# Revit family: SLIM INGROUND 6W SIMETRICO_LKB0326WW.15
name_source: partatom
category: Luminarias
units: mm (PartAtom-declared; Revit-internal decimal feet)

## family parameters
Compartido = No
Corte con vacíos al cargar = No
Cota de conector redondo = Diámetro de uso
Origen de luz = Sí
Punto de cálculo de habitación = No
Se basa en plano de trabajo = Sí
Siempre vertical = No
Tipo de pieza = Normal

## types (1)
- EMP_LKB0326WW.15
    Cambio de temperatura de color de luz atenuada = <Ninguno>
    Comentarios de vataje = 100-240V
    Descripción = LUMINARIA TIPO CIRCULAR PARA EMPOTRAR EN PISO CON CUERPO DE ALUMINIO FUNDIDO A PRESION CUBIERTO CON POLVO GRIS OSCURO, CON CUBIERTA DE ACERO INOXIDABLE Y VIDRIO TEMPLADO DE 8MM, CON 116MM DE DIAMETRO Y 38MM DE PROFUNDIDAD, INSTALACION EMPOTRABLE EN PISO CON POCO ESPACIO, USO PARA INTERIORES COMO EXTERIORES CON IP 67, CUENTA CON 3 LED TIPO OSRAM CON UNA POTENCIA TOTAL DE 6.2W, A UNA TEMPERATURA EN BLANCO CALIDO 3000K CON 388 LUMENES, 89mA EN CORRIENTE DE OPERACIÓN, IK08, IRC 80, DISPONIBLE PARA ATENUAR EN TRIAC, APERTURA A 15 GRADOS POR PROYECTO, FUENTE REMOTA (INCLUIDA) CON 97MM DE LARGO POR 25MM DE ALTO POR 33MM DE ANCHO, ALIMENTADA A 100-240V.
    Elevación por defecto = 0 mm  [stored 0 ft]
    Fabricante = BRILLANT
    Filtro de color = 16777215
    Longitud de símbolo de origen de luz = 500 mm  [stored 1.64042 ft]
    Lámpara = OSRAM
    Modelo = LKB0326WW.15
    Watt per fixture = 6.2
    Ángulo de campo de foco = 15.00°
    Ángulo de enfoque = 15.00°
    Ángulo de inclinación = 30.00°

note: [stored X ft] marks values corroborated as IEEE doubles in the binary element streams (Revit-internal decimal feet)

## geometry (parser evidence)
native form markers: Blend x2
no freeform markers — native parametric forms only
